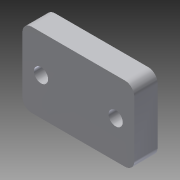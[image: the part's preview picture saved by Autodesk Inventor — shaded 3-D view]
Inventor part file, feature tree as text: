
AUTODESK INVENTOR PART (.ipt)
format: ipt  version: 2014 (Build 180170000, 170)  size: 92,672 bytes
history: native  units: in
note: dims shown in document units (in); Inventor stores cm internally (conversion verified against a paired STEP export)
features: extrude x1, sketch x1
ambient origin geometry x8: Origin, YZ Plane, XZ Plane, XY Plane, X Axis, Y Axis, Z Axis, Center Point
bodies: Solid1 (feature_tree)
feature tree (2):
  extrude  "Extrusion1"  Depth=1.0in
  sketch  "Sketch1"  dims[d0=1.5in d1=1.0in d2=0.19in d3=0.25in d5=0.7874in d7=1.0in d8=0.3937in d10=1.0in d20=0.125in d21=0.3125in d22=0.0in]
